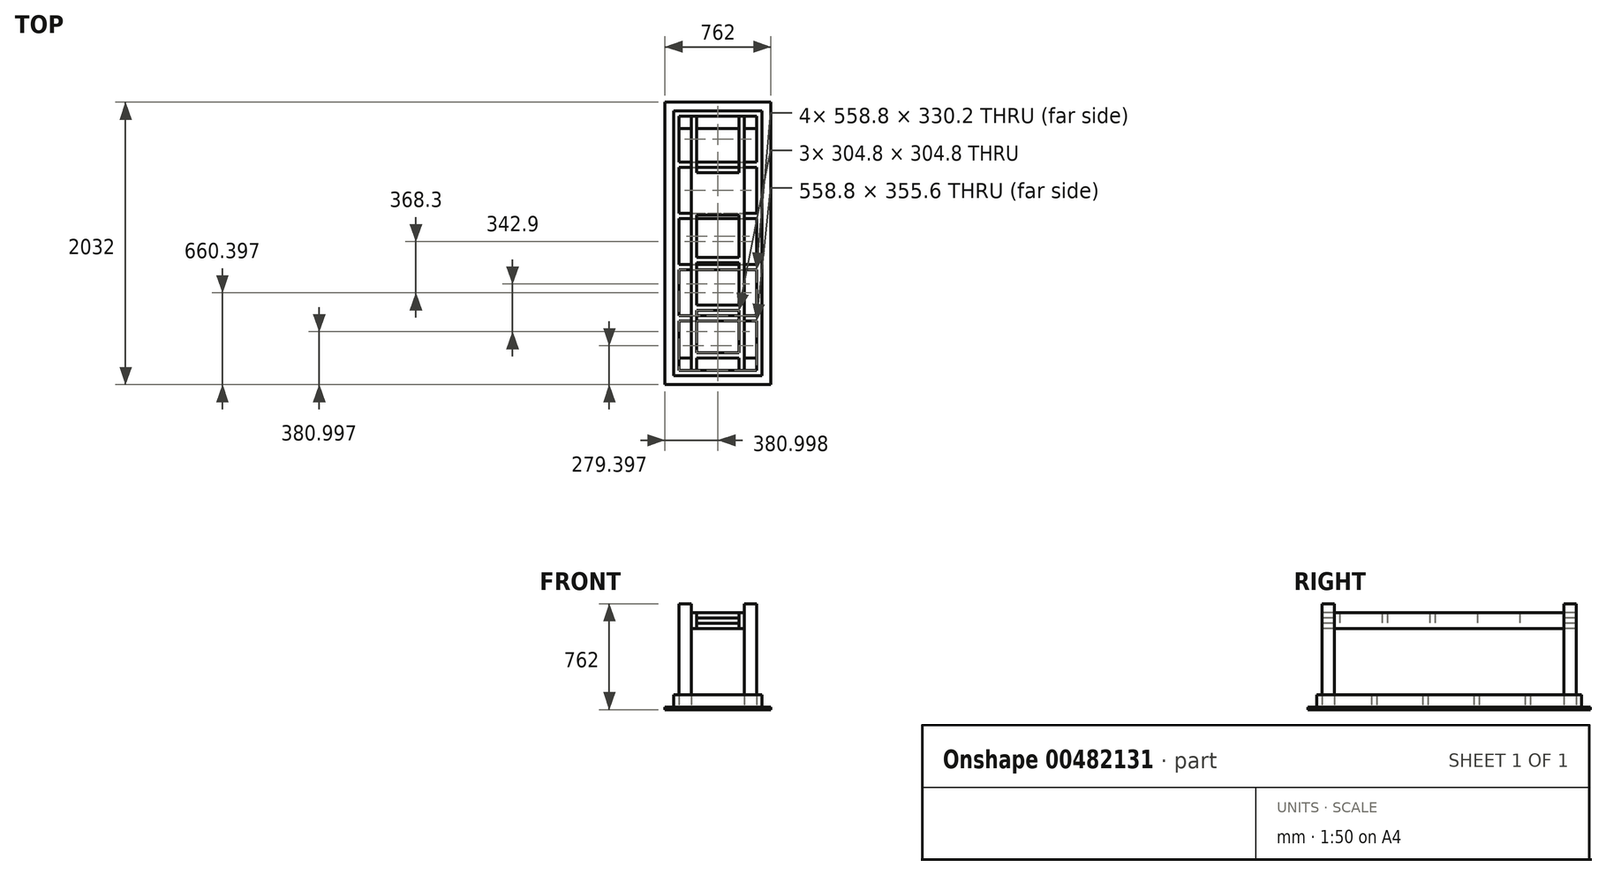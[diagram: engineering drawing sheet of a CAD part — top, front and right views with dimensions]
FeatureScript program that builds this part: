
annotation { "Feature Type Name" : "Feature", "Feature Type Description" : "" }
export const myFeature = defineFeature(function(context is Context, id is Id, definition is map)
    precondition{}
    {
        {
            var Q0;
            Q0=qCreatedBy(makeId("Top.planeOp"),FACE);
            var sketch = newSketch(context, id + "F0", { "sketchPlane" : qUnion([Q0])});
            skLineSegment(sketch, "E0.bottom", {"start": v(-380.18, 1217.87) * mm, "end": v(381.82, 1217.87) * mm});
            skLineSegment(sketch, "E0.top", {"start": v(-380.18, -814.13) * mm, "end": v(381.82, -814.13) * mm});
            skLineSegment(sketch, "E0.left", {"start": v(-380.18, 1217.87) * mm, "end": v(-380.18, -814.13) * mm});
            skLineSegment(sketch, "E0.right", {"start": v(381.82, 1217.87) * mm, "end": v(381.82, -814.13) * mm});
            skSolve(sketch);
        }
        {
            var Q0;
            Q0=makeQuery(id+"F0.imprint","IMPRINT",FACE,{"disambiguationData":[TD([[makeQuery(id+"F0.imprint","IMPRINT",EDGE,{"derivedFrom":sQuery(id+"F0.wireOp",EDGE,"E0.bottom")}),-1.0]])]});
            var sketch = newSketch(context, id + "F1", { "sketchPlane" : qUnion([Q0])});
            skLineSegment(sketch, "E1.bottom", {"start": v(-278.58, -712.53) * mm, "end": v(-189.68, -712.53) * mm});
            skLineSegment(sketch, "E1.top", {"start": v(-278.58, -623.63) * mm, "end": v(-189.68, -623.63) * mm});
            skLineSegment(sketch, "E1.left", {"start": v(-278.58, -712.53) * mm, "end": v(-278.58, -623.63) * mm});
            skLineSegment(sketch, "E1.right", {"start": v(-189.68, -712.53) * mm, "end": v(-189.68, -623.63) * mm});
            skLineSegment(sketch, "E2.bottom", {"start": v(280.22, -712.53) * mm, "end": v(191.32, -712.53) * mm});
            skLineSegment(sketch, "E2.top", {"start": v(280.22, -623.63) * mm, "end": v(191.32, -623.63) * mm});
            skLineSegment(sketch, "E2.left", {"start": v(280.22, -712.53) * mm, "end": v(280.22, -623.63) * mm});
            skLineSegment(sketch, "E2.right", {"start": v(191.32, -712.53) * mm, "end": v(191.32, -623.63) * mm});
            skLineSegment(sketch, "E3.bottom", {"start": v(-189.68, 1027.37) * mm, "end": v(-278.58, 1027.37) * mm});
            skLineSegment(sketch, "E3.top", {"start": v(-189.68, 1116.27) * mm, "end": v(-278.58, 1116.27) * mm});
            skLineSegment(sketch, "E3.left", {"start": v(-189.68, 1027.37) * mm, "end": v(-189.68, 1116.27) * mm});
            skLineSegment(sketch, "E3.right", {"start": v(-278.58, 1027.37) * mm, "end": v(-278.58, 1116.27) * mm});
            skLineSegment(sketch, "E4.bottom", {"start": v(280.22, 1027.37) * mm, "end": v(191.32, 1027.37) * mm});
            skLineSegment(sketch, "E4.top", {"start": v(280.22, 1116.27) * mm, "end": v(191.32, 1116.27) * mm});
            skLineSegment(sketch, "E4.left", {"start": v(280.22, 1027.37) * mm, "end": v(280.22, 1116.27) * mm});
            skLineSegment(sketch, "E4.right", {"start": v(191.32, 1027.37) * mm, "end": v(191.32, 1116.27) * mm});
            skLineSegment(sketch, "E5.bottom", {"start": v(-278.58, -750.63) * mm, "end": v(280.22, -750.63) * mm});
            skLineSegment(sketch, "E5.top", {"start": v(-278.58, -712.53) * mm, "end": v(280.22, -712.53) * mm});
            skLineSegment(sketch, "E5.left", {"start": v(-278.58, -750.63) * mm, "end": v(-278.58, -712.53) * mm});
            skLineSegment(sketch, "E5.right", {"start": v(280.22, -750.63) * mm, "end": v(280.22, -712.53) * mm});
            skLineSegment(sketch, "E6.bottom", {"start": v(-316.68, -750.63) * mm, "end": v(-278.58, -750.63) * mm});
            skLineSegment(sketch, "E6.top", {"start": v(-316.68, 1154.37) * mm, "end": v(-278.58, 1154.37) * mm});
            skLineSegment(sketch, "E6.left", {"start": v(-316.68, -750.63) * mm, "end": v(-316.68, 1154.37) * mm});
            skLineSegment(sketch, "E6.right", {"start": v(-278.58, -750.63) * mm, "end": v(-278.58, 1154.37) * mm});
            skLineSegment(sketch, "E7.bottom", {"start": v(318.32, -750.63) * mm, "end": v(280.22, -750.63) * mm});
            skLineSegment(sketch, "E7.top", {"start": v(318.32, 1154.37) * mm, "end": v(280.22, 1154.37) * mm});
            skLineSegment(sketch, "E7.left", {"start": v(318.32, -750.63) * mm, "end": v(318.32, 1154.37) * mm});
            skLineSegment(sketch, "E7.right", {"start": v(280.22, -750.63) * mm, "end": v(280.22, 1154.37) * mm});
            skLineSegment(sketch, "E8.bottom", {"start": v(-278.58, 1154.37) * mm, "end": v(280.22, 1154.37) * mm});
            skLineSegment(sketch, "E8.top", {"start": v(-278.58, 1116.27) * mm, "end": v(280.22, 1116.27) * mm});
            skLineSegment(sketch, "E8.left", {"start": v(-278.58, 1154.37) * mm, "end": v(-278.58, 1116.27) * mm});
            skLineSegment(sketch, "E8.right", {"start": v(280.22, 1154.37) * mm, "end": v(280.22, 1116.27) * mm});
            skLineSegment(sketch, "E9.bottom", {"start": v(-278.58, 786.07) * mm, "end": v(280.22, 786.07) * mm});
            skLineSegment(sketch, "E9.top", {"start": v(-278.58, 747.97) * mm, "end": v(280.22, 747.97) * mm});
            skLineSegment(sketch, "E9.left", {"start": v(-278.58, 786.07) * mm, "end": v(-278.58, 747.97) * mm});
            skLineSegment(sketch, "E9.right", {"start": v(280.22, 786.07) * mm, "end": v(280.22, 747.97) * mm});
            skLineSegment(sketch, "E10.bottom", {"start": v(-278.58, 417.77) * mm, "end": v(280.22, 417.77) * mm});
            skLineSegment(sketch, "E10.top", {"start": v(-278.58, 379.67) * mm, "end": v(280.22, 379.67) * mm});
            skLineSegment(sketch, "E10.left", {"start": v(-278.58, 417.77) * mm, "end": v(-278.58, 379.67) * mm});
            skLineSegment(sketch, "E10.right", {"start": v(280.22, 417.77) * mm, "end": v(280.22, 379.67) * mm});
            skLineSegment(sketch, "E11.bottom", {"start": v(-278.58, 49.47) * mm, "end": v(280.22, 49.47) * mm});
            skLineSegment(sketch, "E11.top", {"start": v(-278.58, 11.37) * mm, "end": v(280.22, 11.37) * mm});
            skLineSegment(sketch, "E11.left", {"start": v(-278.58, 49.47) * mm, "end": v(-278.58, 11.37) * mm});
            skLineSegment(sketch, "E11.right", {"start": v(280.22, 49.47) * mm, "end": v(280.22, 11.37) * mm});
            skLineSegment(sketch, "E12.bottom", {"start": v(-278.58, -318.83) * mm, "end": v(280.22, -318.83) * mm});
            skLineSegment(sketch, "E12.top", {"start": v(-278.58, -356.93) * mm, "end": v(280.22, -356.93) * mm});
            skLineSegment(sketch, "E12.left", {"start": v(-278.58, -318.83) * mm, "end": v(-278.58, -356.93) * mm});
            skLineSegment(sketch, "E12.right", {"start": v(280.22, -318.83) * mm, "end": v(280.22, -356.93) * mm});
            skSolve(sketch);
        }
        {
            var Q0;
            Q0=makeQuery(id+"F0.imprint","IMPRINT",FACE,{"disambiguationData":[TD([[makeQuery(id+"F0.imprint","IMPRINT",EDGE,{"derivedFrom":sQuery(id+"F0.wireOp",EDGE,"E0.bottom")}),-1.0]])]});
            var sketch = newSketch(context, id + "F2", { "sketchPlane" : qUnion([Q0])});
            skLineSegment(sketch, "E13.bottom", {"start": v(-189.68, 1116.27) * mm, "end": v(-151.58, 1116.27) * mm});
            skLineSegment(sketch, "E13.top", {"start": v(-189.68, -712.53) * mm, "end": v(-151.58, -712.53) * mm});
            skLineSegment(sketch, "E13.left", {"start": v(-189.68, 1116.27) * mm, "end": v(-189.68, -712.53) * mm});
            skLineSegment(sketch, "E13.right", {"start": v(-151.58, 1116.27) * mm, "end": v(-151.58, -712.53) * mm});
            skLineSegment(sketch, "E14.bottom", {"start": v(191.32, 1116.27) * mm, "end": v(153.22, 1116.27) * mm});
            skLineSegment(sketch, "E14.top", {"start": v(191.32, -712.53) * mm, "end": v(153.22, -712.53) * mm});
            skLineSegment(sketch, "E14.left", {"start": v(191.32, 1116.27) * mm, "end": v(191.32, -712.53) * mm});
            skLineSegment(sketch, "E14.right", {"start": v(153.22, 1116.27) * mm, "end": v(153.22, -712.53) * mm});
            skLineSegment(sketch, "E15.bottom", {"start": v(-151.58, -712.53) * mm, "end": v(153.22, -712.53) * mm});
            skLineSegment(sketch, "E15.top", {"start": v(-151.58, -623.63) * mm, "end": v(153.22, -623.63) * mm});
            skLineSegment(sketch, "E15.left", {"start": v(-151.58, -712.53) * mm, "end": v(-151.58, -623.63) * mm});
            skLineSegment(sketch, "E15.right", {"start": v(153.22, -712.53) * mm, "end": v(153.22, -623.63) * mm});
            skLineSegment(sketch, "E16.bottom", {"start": v(-151.58, 1116.27) * mm, "end": v(153.22, 1116.27) * mm});
            skLineSegment(sketch, "E16.top", {"start": v(-151.58, 1027.37) * mm, "end": v(153.22, 1027.37) * mm});
            skLineSegment(sketch, "E16.left", {"start": v(-151.58, 1116.27) * mm, "end": v(-151.58, 1027.37) * mm});
            skLineSegment(sketch, "E16.right", {"start": v(153.22, 1116.27) * mm, "end": v(153.22, 1027.37) * mm});
            skLineSegment(sketch, "E17.top", {"start": v(-151.58, 988.15) * mm, "end": v(153.22, 988.15) * mm});
            skLineSegment(sketch, "E17.left", {"start": v(-151.58, 1027.37) * mm, "end": v(-151.58, 988.15) * mm});
            skLineSegment(sketch, "E17.right", {"start": v(153.22, 1027.37) * mm, "end": v(153.22, 988.15) * mm});
            skLineSegment(sketch, "E18.bottom", {"start": v(-151.58, 709.87) * mm, "end": v(153.22, 709.87) * mm});
            skLineSegment(sketch, "E18.top", {"start": v(-151.58, 747.97) * mm, "end": v(153.22, 747.97) * mm});
            skLineSegment(sketch, "E18.left", {"start": v(-151.58, 747.97) * mm, "end": v(-151.58, 709.87) * mm});
            skLineSegment(sketch, "E18.right", {"start": v(153.22, 747.97) * mm, "end": v(153.22, 709.87) * mm});
            skLineSegment(sketch, "E19.bottom", {"start": v(-151.58, 443.17) * mm, "end": v(153.22, 443.17) * mm});
            skLineSegment(sketch, "E19.top", {"start": v(-151.58, 405.07) * mm, "end": v(153.22, 405.07) * mm});
            skLineSegment(sketch, "E19.left", {"start": v(-151.58, 443.17) * mm, "end": v(-151.58, 405.07) * mm});
            skLineSegment(sketch, "E19.right", {"start": v(153.22, 443.17) * mm, "end": v(153.22, 405.07) * mm});
            skLineSegment(sketch, "E20.bottom", {"start": v(-151.58, 100.27) * mm, "end": v(153.22, 100.27) * mm});
            skLineSegment(sketch, "E20.top", {"start": v(-151.58, 62.17) * mm, "end": v(153.22, 62.17) * mm});
            skLineSegment(sketch, "E20.left", {"start": v(-151.58, 100.27) * mm, "end": v(-151.58, 62.17) * mm});
            skLineSegment(sketch, "E20.right", {"start": v(153.22, 100.27) * mm, "end": v(153.22, 62.17) * mm});
            skLineSegment(sketch, "E21.bottom", {"start": v(-151.58, -242.63) * mm, "end": v(153.22, -242.63) * mm});
            skLineSegment(sketch, "E21.top", {"start": v(-151.58, -280.73) * mm, "end": v(153.22, -280.73) * mm});
            skLineSegment(sketch, "E21.left", {"start": v(-151.58, -242.63) * mm, "end": v(-151.58, -280.73) * mm});
            skLineSegment(sketch, "E21.right", {"start": v(153.22, -242.63) * mm, "end": v(153.22, -280.73) * mm});
            skLineSegment(sketch, "E22.bottom", {"start": v(-151.58, -585.53) * mm, "end": v(153.22, -585.53) * mm});
            skLineSegment(sketch, "E22.left", {"start": v(-151.58, -585.53) * mm, "end": v(-151.58, -623.63) * mm});
            skLineSegment(sketch, "E22.right", {"start": v(153.22, -585.53) * mm, "end": v(153.22, -623.63) * mm});
            skSolve(sketch);
        }
        {
            var Q0;
            Q0=makeQuery(id+"F2.imprint","IMPRINT",FACE,{"disambiguationData":[TD([[makeQuery(id+"F2.imprint","IMPRINT",EDGE,{"derivedFrom":sQuery(id+"F2.wireOp",EDGE,"E13.bottom")}),-1.0]])]});
            var Q1;
            Q1=makeQuery(id+"F2.imprint","IMPRINT",FACE,{"disambiguationData":[TD([[makeQuery(id+"F2.imprint","IMPRINT",EDGE,{"derivedFrom":sQuery(id+"F2.wireOp",EDGE,"E16.top")}),-1.0]])]});
            var Q2;
            Q2=makeQuery(id+"F2.imprint","IMPRINT",FACE,{"disambiguationData":[TD([[makeQuery(id+"F2.imprint","IMPRINT",EDGE,{"derivedFrom":sQuery(id+"F2.wireOp",EDGE,"E14.bottom")}),1.0]])]});
            var Q3;
            Q3=makeQuery(id+"F2.imprint","IMPRINT",FACE,{"disambiguationData":[TD([[makeQuery(id+"F2.imprint","IMPRINT",EDGE,{"derivedFrom":sQuery(id+"F2.wireOp",EDGE,"E18.bottom")}),-1.0]])]});
            var Q4;
            Q4=makeQuery(id+"F2.imprint","IMPRINT",FACE,{"disambiguationData":[TD([[makeQuery(id+"F2.imprint","IMPRINT",EDGE,{"derivedFrom":sQuery(id+"F2.wireOp",EDGE,"E19.bottom")}),-1.0]])]});
            var Q5;
            Q5=makeQuery(id+"F2.imprint","IMPRINT",FACE,{"disambiguationData":[TD([[makeQuery(id+"F2.imprint","IMPRINT",EDGE,{"derivedFrom":sQuery(id+"F2.wireOp",EDGE,"E20.bottom")}),-1.0]])]});
            var Q6;
            Q6=makeQuery(id+"F2.imprint","IMPRINT",FACE,{"disambiguationData":[TD([[makeQuery(id+"F2.imprint","IMPRINT",EDGE,{"derivedFrom":sQuery(id+"F2.wireOp",EDGE,"E21.bottom")}),-1.0]])]});
            var Q7;
            Q7=makeQuery(id+"F2.imprint","IMPRINT",FACE,{"disambiguationData":[TD([[makeQuery(id+"F2.imprint","IMPRINT",EDGE,{"derivedFrom":sQuery(id+"F2.wireOp",EDGE,"E22.bottom")}),-1.0]])]});
            extrude(context, id + "F3", {"entities" : qUnion([Q0, Q1, Q2, Q3, Q4, Q5, Q6, Q7]), "depth" : 698.5 * mm, "hasSecondDirection" : true, "secondDirectionOppositeDirection" : false, "secondDirectionDepth" : 584.2 * mm});
        }
        {
            var Q0;
            Q0=makeQuery(id+"F0.imprint","IMPRINT",FACE,{"disambiguationData":[TD([[makeQuery(id+"F0.imprint","IMPRINT",EDGE,{"derivedFrom":sQuery(id+"F0.wireOp",EDGE,"E0.bottom")}),-1.0]])]});
            extrude(context, id + "F4", {"entities" : qUnion([Q0]), "depth" : 19.05 * mm});
        }
        {
            var Q0;
            {var subQ8=sQuery(id+"F1.wireOp",EDGE,"E6.bottom");Q0=makeQuery(id+"F1.imprint","IMPRINT",FACE,{"disambiguationData":[TD([[makeQuery(id+"F1.imprint","IMPRINT",EDGE,{"derivedFrom":subQ8}),1.0]])]});}
            var Q1;
            {var subQ7=sQuery(id+"F1.wireOp",EDGE,"E5.bottom");Q1=makeQuery(id+"F1.imprint","IMPRINT",FACE,{"disambiguationData":[TD([[makeQuery(id+"F1.imprint","IMPRINT",EDGE,{"derivedFrom":subQ7}),1.0]])]});}
            var Q2;
            {var subQ8=sQuery(id+"F1.wireOp",EDGE,"E7.bottom");Q2=makeQuery(id+"F1.imprint","IMPRINT",FACE,{"disambiguationData":[TD([[makeQuery(id+"F1.imprint","IMPRINT",EDGE,{"derivedFrom":subQ8}),-1.0]])]});}
            var Q3;
            Q3=makeQuery(id+"F1.imprint","IMPRINT",FACE,{"disambiguationData":[TD([[makeQuery(id+"F1.imprint","IMPRINT",EDGE,{"derivedFrom":sQuery(id+"F1.wireOp",EDGE,"E12.bottom")}),-1.0]])]});
            var Q4;
            Q4=makeQuery(id+"F1.imprint","IMPRINT",FACE,{"disambiguationData":[TD([[makeQuery(id+"F1.imprint","IMPRINT",EDGE,{"derivedFrom":sQuery(id+"F1.wireOp",EDGE,"E11.bottom")}),-1.0]])]});
            var Q5;
            Q5=makeQuery(id+"F1.imprint","IMPRINT",FACE,{"disambiguationData":[TD([[makeQuery(id+"F1.imprint","IMPRINT",EDGE,{"derivedFrom":sQuery(id+"F1.wireOp",EDGE,"E10.bottom")}),-1.0]])]});
            var Q6;
            Q6=makeQuery(id+"F1.imprint","IMPRINT",FACE,{"disambiguationData":[TD([[makeQuery(id+"F1.imprint","IMPRINT",EDGE,{"derivedFrom":sQuery(id+"F1.wireOp",EDGE,"E9.bottom")}),-1.0]])]});
            var Q7;
            Q7=makeQuery(id+"F1.imprint","IMPRINT",FACE,{"disambiguationData":[TD([[makeQuery(id+"F1.imprint","IMPRINT",EDGE,{"derivedFrom":sQuery(id+"F1.wireOp",EDGE,"E8.bottom")}),-1.0]])]});
            extrude(context, id + "F5", {"entities" : qUnion([Q0, Q1, Q2, Q3, Q4, Q5, Q6, Q7]), "depth" : 107.95 * mm, "hasSecondDirection" : true, "secondDirectionOppositeDirection" : false, "secondDirectionDepth" : 19.05 * mm});
        }
        {
            var Q0;
            {var subQ0=sQuery(id+"F1.wireOp",EDGE,"E1.top");Q0=makeQuery(id+"F1.imprint","IMPRINT",FACE,{"disambiguationData":[TD([[makeQuery(id+"F1.imprint","IMPRINT",EDGE,{"derivedFrom":subQ0}),-1.0]])]});}
            var Q1;
            {var subQ0=sQuery(id+"F1.wireOp",EDGE,"E2.top");Q1=makeQuery(id+"F1.imprint","IMPRINT",FACE,{"disambiguationData":[TD([[makeQuery(id+"F1.imprint","IMPRINT",EDGE,{"derivedFrom":subQ0}),1.0]])]});}
            var Q2;
            {var subQ0=sQuery(id+"F1.wireOp",EDGE,"E4.bottom");Q2=makeQuery(id+"F1.imprint","IMPRINT",FACE,{"disambiguationData":[TD([[makeQuery(id+"F1.imprint","IMPRINT",EDGE,{"derivedFrom":subQ0}),-1.0]])]});}
            var Q3;
            {var subQ0=sQuery(id+"F1.wireOp",EDGE,"E3.bottom");Q3=makeQuery(id+"F1.imprint","IMPRINT",FACE,{"disambiguationData":[TD([[makeQuery(id+"F1.imprint","IMPRINT",EDGE,{"derivedFrom":subQ0}),-1.0]])]});}
            extrude(context, id + "F6", {"entities" : qUnion([Q0, Q1, Q2, Q3]), "depth" : 762 * mm, "hasSecondDirection" : true, "secondDirectionOppositeDirection" : false, "secondDirectionDepth" : 19.05 * mm});
        }
        {
            var Q0;
            Q0=makeQuery(id+"F2.imprint","IMPRINT",FACE,{"disambiguationData":[TD([[makeQuery(id+"F2.imprint","IMPRINT",EDGE,{"derivedFrom":sQuery(id+"F2.wireOp",EDGE,"E15.bottom")}),1.0]])]});
            var Q1;
            Q1=makeQuery(id+"F2.imprint","IMPRINT",FACE,{"disambiguationData":[TD([[makeQuery(id+"F2.imprint","IMPRINT",EDGE,{"derivedFrom":sQuery(id+"F2.wireOp",EDGE,"E16.bottom")}),-1.0]])]});
            extrude(context, id + "F7", {"entities" : qUnion([Q0, Q1]), "depth" : 660.4 * mm, "hasSecondDirection" : true, "secondDirectionOppositeDirection" : false, "secondDirectionDepth" : 622.3 * mm});
        }
    });
